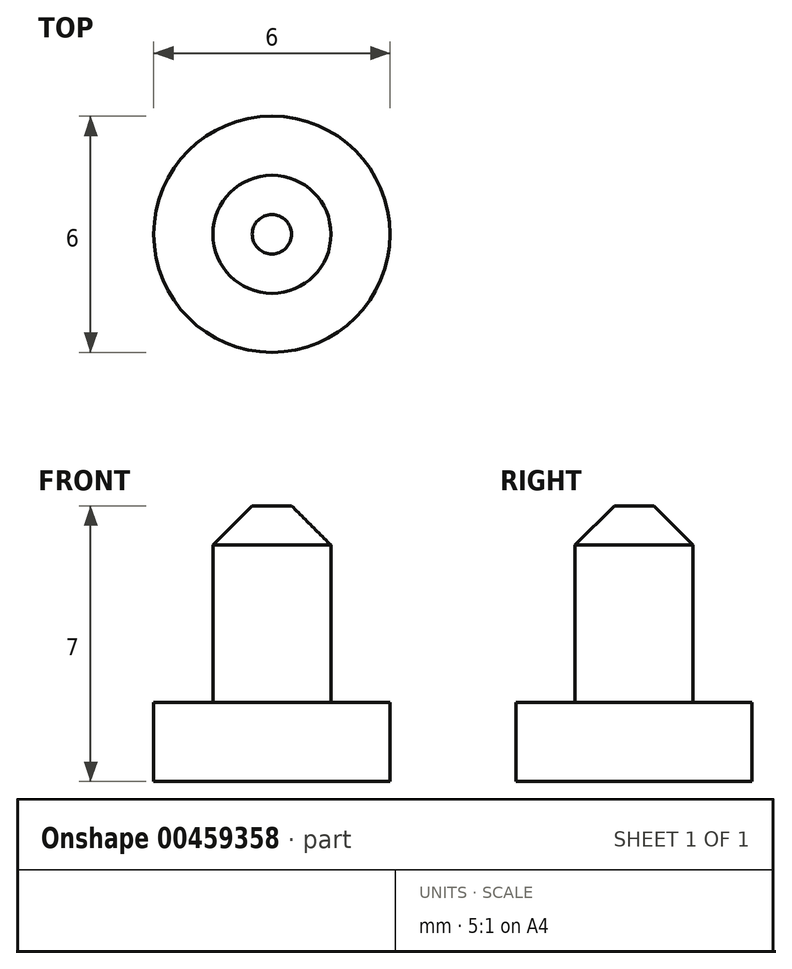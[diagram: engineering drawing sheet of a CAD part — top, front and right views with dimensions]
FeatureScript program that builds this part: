
annotation { "Feature Type Name" : "Feature", "Feature Type Description" : "" }
export const myFeature = defineFeature(function(context is Context, id is Id, definition is map)
    precondition{}
    {
        {
            var Q0;
            Q0=qCreatedBy(makeId("Top.planeOp"),FACE);
            var sketch = newSketch(context, id + "F0", { "sketchPlane" : qUnion([Q0])});
            skCircle(sketch, "E0", {"center": v(0, 0) * mm, "radius": 1.5 * mm});
            skCircle(sketch, "E1", {"center": v(0, 0) * mm, "radius": 3 * mm});
            skSolve(sketch);
        }
        {
            var Q0;
            Q0=makeQuery(id+"F0.imprint","IMPRINT",FACE,{"disambiguationData":[TD([[makeQuery(id+"F0.imprint","IMPRINT",EDGE,{"derivedFrom":sQuery(id+"F0.wireOp",EDGE,"E0")}),-1.0]])]});
            extrude(context, id + "F1", {"entities" : qUnion([Q0]), "depth" : 2 * mm});
        }
        {
            var Q0;
            Q0=makeQuery(id+"F0.imprint","IMPRINT",FACE,{"disambiguationData":[TD([[makeQuery(id+"F0.imprint","IMPRINT",EDGE,{"derivedFrom":sQuery(id+"F0.wireOp",EDGE,"E0")}),1.0]])]});
            extrude(context, id + "F2", {"entities" : qUnion([Q0]), "operationType" : NewBodyOperationType.ADD, "depth" : (2 + 5) * mm});
        }
        {
            var Q0;
            Q0=makeQuery(id+"F2.opExtrude","CAP_FACE",FACE,{"disambiguationData":[OSD([sQuery(id+"F0.wireOp",EDGE,"E0")])],"isStart":false});
            chamfer(context, id + "F3", {"entities" : qUnion([Q0]), "width" : 1 * mm, "tangentPropagation" : true});
        }
    });
